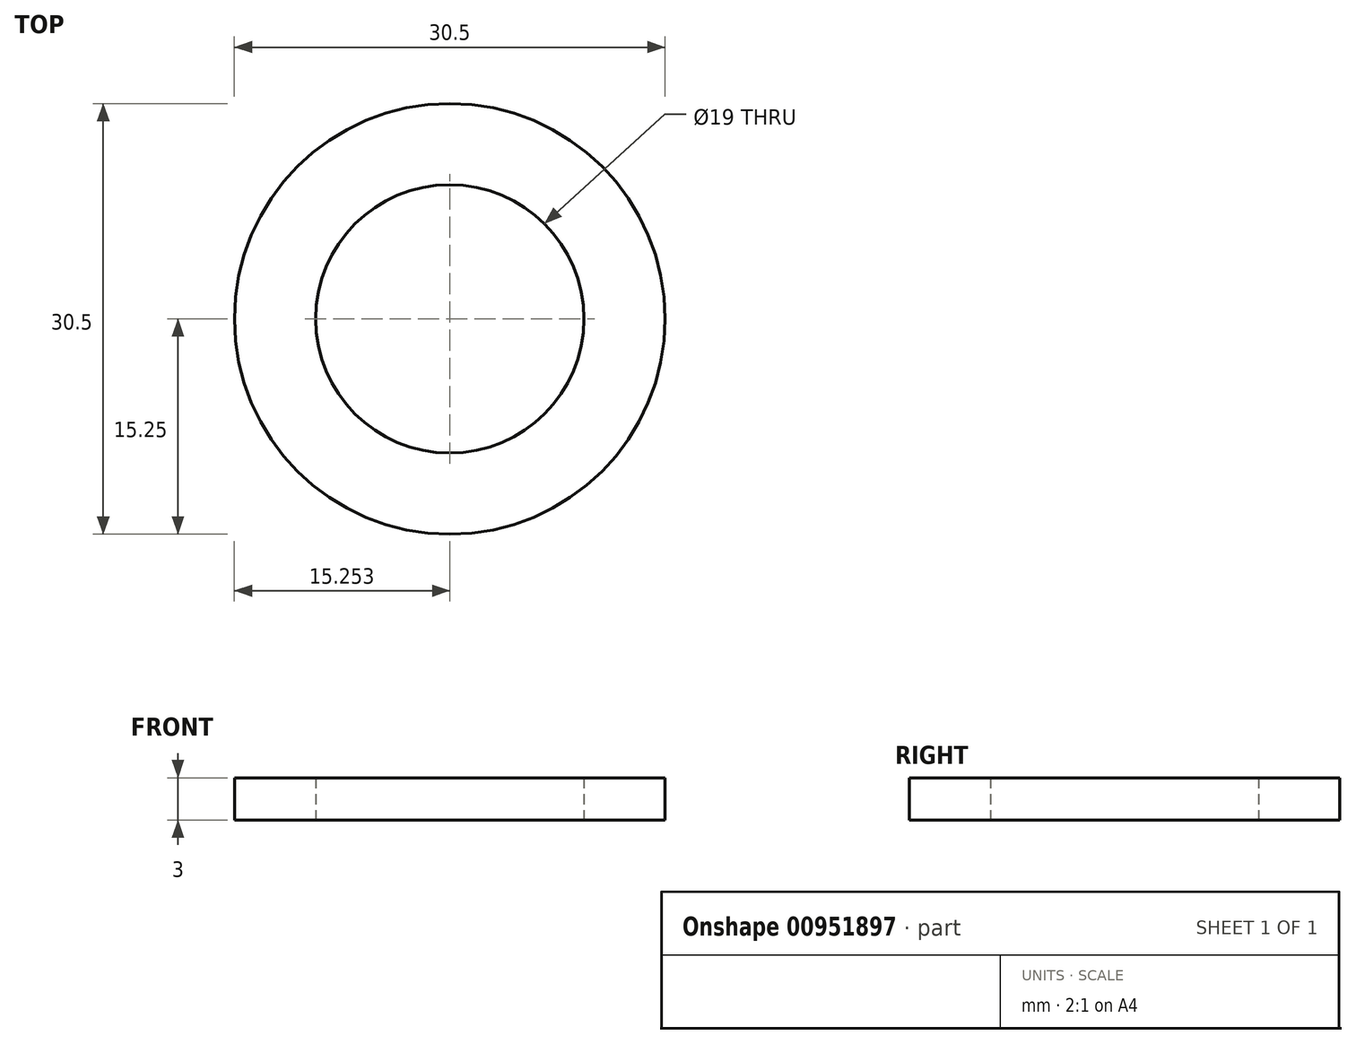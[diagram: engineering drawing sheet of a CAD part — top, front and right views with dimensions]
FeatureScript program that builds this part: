
annotation { "Feature Type Name" : "Feature", "Feature Type Description" : "" }
export const myFeature = defineFeature(function(context is Context, id is Id, definition is map)
    precondition{}
    {
        {
            var Q0;
            Q0=qCreatedBy(makeId("Top.planeOp"),FACE);
            var sketch = newSketch(context, id + "F0", { "sketchPlane" : qUnion([Q0])});
            skCircle(sketch, "E0", {"center": v(-39.15, 0) * mm, "radius": 15.25 * mm});
            skCircle(sketch, "E1", {"center": v(-39.15, 0) * mm, "radius": 28 * mm});
            skCircle(sketch, "E2", {"center": v(-39.15, 0) * mm, "radius": 9.5 * mm});
            skArc(sketch, "E3", {"start": v(-62.03, -10.06) * mm, "mid": v(-53.84, -20.23) * mm, "end": v(-41.65, -24.87) * mm});
            skArc(sketch, "E4", {"start": v(-55.57, -7.96) * mm, "mid": v(-49.87, -14.76) * mm, "end": v(-41.65, -18.08) * mm});
            skLineSegment(sketch, "E5", {"start": v(-41.65, -24.87) * mm, "end": v(-41.65, -18.08) * mm});
            skLineSegment(sketch, "E6", {"start": v(-36.65, -18.08) * mm, "end": v(-36.65, -24.87) * mm});
            skLineSegment(sketch, "E7", {"start": v(-55.57, -7.96) * mm, "end": v(-62.03, -10.06) * mm});
            skLineSegment(sketch, "E8", {"start": v(-57.11, -3.2) * mm, "end": v(-63.58, -5.3) * mm});
            skLineSegment(sketch, "E9", {"start": v(-51.8, 13.16) * mm, "end": v(-55.79, 18.65) * mm});
            skLineSegment(sketch, "E10", {"start": v(-55.79, 18.65) * mm, "end": v(-56.02, 18.38) * mm});
            skLineSegment(sketch, "E11", {"start": v(-47.75, 16.1) * mm, "end": v(-51.74, 21.6) * mm});
            skLineSegment(sketch, "E12", {"start": v(-30.54, 16.1) * mm, "end": v(-26.55, 21.6) * mm});
            skLineSegment(sketch, "E13", {"start": v(-26.5, 13.16) * mm, "end": v(-22.5, 18.65) * mm});
            skLineSegment(sketch, "E14", {"start": v(-21.18, -3.2) * mm, "end": v(-14.72, -5.3) * mm});
            skPoint(sketch, "E14.startSnap0", {"position": v(-21.18, -5.84) * mm});
            skLineSegment(sketch, "E15", {"start": v(-22.73, -7.96) * mm, "end": v(-16.26, -10.06) * mm});
            skPoint(sketch, "E16.orphan", {"position": v(-3.22, -11.67) * mm});
            skArc(sketch, "E17.trimOffspring", {"start": v(-51.8, 13.16) * mm, "mid": v(-56.5, 5.64) * mm, "end": v(-57.11, -3.2) * mm});
            skArc(sketch, "E18.trimOffspring", {"start": v(-55.79, 18.65) * mm, "mid": v(-62.92, 7.73) * mm, "end": v(-63.58, -5.3) * mm});
            skArc(sketch, "E19.trimOffspring", {"start": v(-30.54, 16.1) * mm, "mid": v(-39.15, 18.25) * mm, "end": v(-47.75, 16.1) * mm});
            skArc(sketch, "E20.trimOffspring", {"start": v(-26.55, 21.6) * mm, "mid": v(-39.15, 25) * mm, "end": v(-51.74, 21.6) * mm});
            skArc(sketch, "E21.trimOffspring", {"start": v(-21.18, -3.2) * mm, "mid": v(-21.79, 5.64) * mm, "end": v(-26.5, 13.16) * mm});
            skArc(sketch, "E22.trimOffspring", {"start": v(-14.72, -5.3) * mm, "mid": v(-15.37, 7.73) * mm, "end": v(-22.5, 18.65) * mm});
            skArc(sketch, "E23.trimOffspring", {"start": v(-36.65, -24.87) * mm, "mid": v(-24.45, -20.23) * mm, "end": v(-16.26, -10.06) * mm});
            skArc(sketch, "E24.trimOffspring", {"start": v(-36.65, -18.08) * mm, "mid": v(-28.42, -14.76) * mm, "end": v(-22.73, -7.96) * mm});
            skSolve(sketch);
        }
        {
            var Q0;
            Q0=makeQuery(id+"F0.imprint","IMPRINT",FACE,{"disambiguationData":[TD([[makeQuery(id+"F0.imprint","IMPRINT",EDGE,{"derivedFrom":sQuery(id+"F0.wireOp",EDGE,"E0")}),1.0]])]});
            var Q1;
            Q1=makeQuery(id+"F0.imprint","IMPRINT",FACE,{"disambiguationData":[TD([[makeQuery(id+"F0.imprint","IMPRINT",EDGE,{"derivedFrom":sQuery(id+"F0.wireOp",EDGE,"gZvZpgXt-Y5T6-j4Jx-lpFE-VRuZzmW9fOwK")}),-1.0]])]});
            extrude(context, id + "F1", {"entities" : qUnion([Q0, Q1]), "depth" : 3 * mm, "offsetDistance" : 25 * mm});
        }
    });
